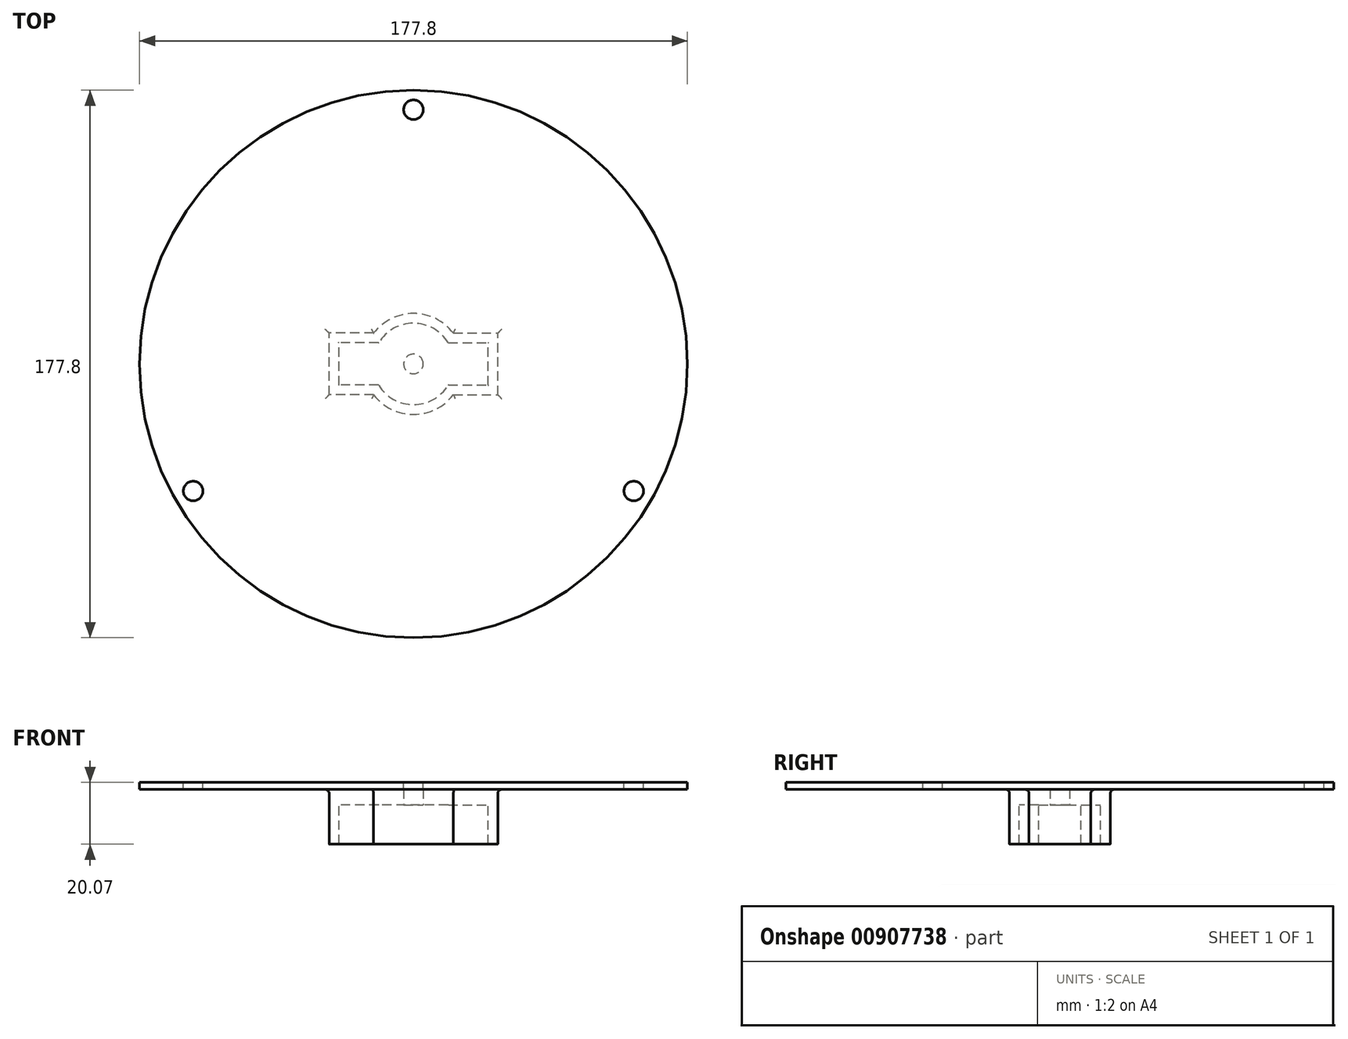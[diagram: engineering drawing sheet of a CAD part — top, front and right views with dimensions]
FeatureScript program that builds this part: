
annotation { "Feature Type Name" : "Feature", "Feature Type Description" : "" }
export const myFeature = defineFeature(function(context is Context, id is Id, definition is map)
    precondition{}
    {
        {
            var Q0;
            Q0=qCreatedBy(makeId("Top.planeOp"),FACE);
            var sketch = newSketch(context, id + "F0", { "sketchPlane" : qUnion([Q0])});
            skCircle(sketch, "E0", {"center": v(0, 0) * mm, "radius": 88.9 * mm});
            skSolve(sketch);
        }
        {
            var Q0;
            Q0=makeQuery(id+"F0.imprint","IMPRINT",FACE,{"disambiguationData":[TD([[makeQuery(id+"F0.imprint","IMPRINT",EDGE,{"derivedFrom":sQuery(id+"F0.wireOp",EDGE,"E0")}),1.0]])]});
            extrude(context, id + "F1", {"entities" : qUnion([Q0]), "depth" : 2.3 * mm, "offsetDistance" : 25.4 * mm});
        }
        {
            var Q0;
            Q0=makeQuery(id+"F1.opExtrude","CAP_FACE",FACE,{"disambiguationData":[OSD([sQuery(id+"F0.wireOp",EDGE,"E0")])],"isStart":false});
            var sketch = newSketch(context, id + "F2", { "sketchPlane" : qUnion([Q0])});
            skCircle(sketch, "E1", {"center": v(0, 82.55) * mm, "radius": 3.18 * mm});
            skCircle(sketch, "E2.1.0", {"center": v(-71.5, -41.27) * mm, "radius": 3.18 * mm});
            skCircle(sketch, "E2.2.0", {"center": v(71.5, -41.28) * mm, "radius": 3.18 * mm});
            skPoint(sketch, "E2.center", {"position": v(0, 0) * mm});
            skSolve(sketch);
        }
        {
            var Q0;
            Q0 = qSketchRegion(id + "F2", true);
            extrude(context, id + "F3", {"entities" : qUnion([Q0]), "operationType" : NewBodyOperationType.REMOVE, "oppositeDirection" : true, "depth" : 25.4 * mm, "offsetDistance" : 25.4 * mm});
        }
        {
            var Q0;
            Q0=makeQuery(id+"F1.opExtrude","CAP_FACE",FACE,{"disambiguationData":[OSD([sQuery(id+"F0.wireOp",EDGE,"E0")])],"isStart":true});
            var sketch = newSketch(context, id + "F4", { "sketchPlane" : qUnion([Q0])});
            skArc(sketch, "E3", {"start": v(0, 12.7) * mm, "mid": v(-6.35, 11) * mm, "end": v(-11, 6.35) * mm});
            skLineSegment(sketch, "E4.bottom", {"start": v(-11, 6.35) * mm, "end": v(-23.7, 6.35) * mm});
            skLineSegment(sketch, "E4.top", {"start": v(-11, -6.35) * mm, "end": v(-23.7, -6.35) * mm});
            skLineSegment(sketch, "E4.right", {"start": v(-23.7, 6.35) * mm, "end": v(-23.7, -6.35) * mm});
            skArc(sketch, "E5.trimOffspring", {"start": v(-11, -6.35) * mm, "mid": v(-6.35, -11) * mm, "end": v(0, -12.7) * mm});
            skArc(sketch, "E6.MirrorCS", {"start": v(0, 12.7) * mm, "mid": v(6.35, 11) * mm, "end": v(11, 6.35) * mm});
            skLineSegment(sketch, "E7.MirrorCS", {"start": v(11, 6.35) * mm, "end": v(23.7, 6.35) * mm});
            skLineSegment(sketch, "E8.MirrorCS", {"start": v(23.7, 6.35) * mm, "end": v(23.7, -6.35) * mm});
            skLineSegment(sketch, "E9.MirrorCS", {"start": v(11, -6.35) * mm, "end": v(23.7, -6.35) * mm});
            skArc(sketch, "E10.MirrorCS", {"start": v(11, -6.35) * mm, "mid": v(6.35, -11) * mm, "end": v(0, -12.7) * mm});
            skArc(sketch, "E11.0", {"start": v(0, 13.2) * mm, "mid": v(-6.48, 11.51) * mm, "end": v(-11.29, 6.86) * mm});
            skArc(sketch, "E11.1", {"start": v(0, 13.2) * mm, "mid": v(6.48, 11.51) * mm, "end": v(11.29, 6.86) * mm});
            skLineSegment(sketch, "E11.2", {"start": v(-11.29, 6.86) * mm, "end": v(-24.2, 6.86) * mm});
            skLineSegment(sketch, "E11.3", {"start": v(11.29, 6.86) * mm, "end": v(24.2, 6.86) * mm});
            skLineSegment(sketch, "E11.4", {"start": v(24.2, 6.86) * mm, "end": v(24.2, -6.86) * mm});
            skLineSegment(sketch, "E11.5", {"start": v(11.29, -6.86) * mm, "end": v(24.2, -6.86) * mm});
            skLineSegment(sketch, "E11.6", {"start": v(-24.2, 6.86) * mm, "end": v(-24.2, -6.86) * mm});
            skLineSegment(sketch, "E11.7", {"start": v(-11.29, -6.86) * mm, "end": v(-24.2, -6.86) * mm});
            skArc(sketch, "E11.8", {"start": v(-11.29, -6.86) * mm, "mid": v(-6.48, -11.51) * mm, "end": v(0, -13.2) * mm});
            skArc(sketch, "E11.9", {"start": v(11.29, -6.86) * mm, "mid": v(6.48, -11.51) * mm, "end": v(0, -13.2) * mm});
            skArc(sketch, "E12.0", {"start": v(0, 16.38) * mm, "mid": v(-7.21, 14.7) * mm, "end": v(-12.95, 10.03) * mm});
            skArc(sketch, "E12.1", {"start": v(0, 16.38) * mm, "mid": v(7.21, 14.7) * mm, "end": v(12.95, 10.03) * mm});
            skLineSegment(sketch, "E12.2", {"start": v(-12.95, 10.03) * mm, "end": v(-27.37, 10.03) * mm});
            skLineSegment(sketch, "E12.3", {"start": v(12.95, 10.03) * mm, "end": v(27.37, 10.03) * mm});
            skLineSegment(sketch, "E12.4", {"start": v(27.37, 10.03) * mm, "end": v(27.37, -10.03) * mm});
            skLineSegment(sketch, "E12.5", {"start": v(12.95, -10.03) * mm, "end": v(27.37, -10.03) * mm});
            skLineSegment(sketch, "E12.6", {"start": v(-27.37, 10.03) * mm, "end": v(-27.37, -10.03) * mm});
            skLineSegment(sketch, "E12.7", {"start": v(-12.95, -10.03) * mm, "end": v(-27.37, -10.03) * mm});
            skArc(sketch, "E12.8", {"start": v(-12.95, -10.03) * mm, "mid": v(-7.21, -14.7) * mm, "end": v(0, -16.38) * mm});
            skArc(sketch, "E12.9", {"start": v(12.95, -10.03) * mm, "mid": v(7.21, -14.7) * mm, "end": v(0, -16.38) * mm});
            skSolve(sketch);
        }
        {
            var Q0;
            Q0=makeQuery(id+"F4.imprint","IMPRINT",FACE,{"disambiguationData":[TD([[makeQuery(id+"F4.imprint","IMPRINT",EDGE,{"derivedFrom":sQuery(id+"F4.wireOp",EDGE,"E11.0")}),-1.0]])]});
            extrude(context, id + "F5", {"entities" : qUnion([Q0]), "operationType" : NewBodyOperationType.ADD, "depth" : 17.78 * mm, "offsetDistance" : 25.4 * mm});
        }
        {
            var Q0;
            Q0=makeQuery(id+"F5.boolean.opBoolean","SPLIT",FACE,{"disambiguationData":[TD([makeQuery(id+"F5.opExtrude","SWEPT_FACE",FACE,{"disambiguationData":[OSD([sQuery(id+"F4.wireOp",EDGE,"E11.2")])]})])],"derivedFrom":makeQuery(id+"F1.opExtrude","CAP_FACE",FACE,{"disambiguationData":[OSD([sQuery(id+"F0.wireOp",EDGE,"E0")])],"isStart":true})});
            extrude(context, id + "F6", {"entities" : qUnion([Q0]), "operationType" : NewBodyOperationType.ADD, "depth" : 5.08 * mm, "offsetDistance" : 25.4 * mm});
        }
        {
            var Q0;
            Q0=makeQuery(id+"F6.opExtrude","CAP_FACE",FACE,{"disambiguationData":[OSD([sQuery(id+"F0.wireOp",EDGE,"E0")])],"isStart":false});
            var sketch = newSketch(context, id + "F7", { "sketchPlane" : qUnion([Q0])});
            skCircle(sketch, "E13", {"center": v(0, 0) * mm, "radius": 3.18 * mm});
            skSolve(sketch);
        }
        {
            var Q0;
            Q0 = qSketchRegion(id + "F7", true);
            extrude(context, id + "F8", {"entities" : qUnion([Q0]), "operationType" : NewBodyOperationType.REMOVE, "oppositeDirection" : true, "depth" : 5.08 * mm, "offsetDistance" : 25.4 * mm});
        }
        {
            var Q0;
            Q0=makeQuery(id+"F5.opExtrude","SWEPT_EDGE",EDGE,{"disambiguationData":[OSD([sQuery(id+"F4.wireOp",EDGE,"E11.1"),sQuery(id+"F4.wireOp",EDGE,"E11.3")])]});
            var Q1;
            Q1=makeQuery(id+"F5.opExtrude","SWEPT_EDGE",EDGE,{"disambiguationData":[OSD([sQuery(id+"F4.wireOp",EDGE,"E11.0"),sQuery(id+"F4.wireOp",EDGE,"E11.2")])]});
            var Q2;
            Q2=makeQuery(id+"F5.opExtrude","SWEPT_EDGE",EDGE,{"disambiguationData":[OSD([sQuery(id+"F4.wireOp",EDGE,"E11.5"),sQuery(id+"F4.wireOp",EDGE,"E11.9")])]});
            var Q3;
            Q3=makeQuery(id+"F5.opExtrude","SWEPT_EDGE",EDGE,{"disambiguationData":[OSD([sQuery(id+"F4.wireOp",EDGE,"E11.7"),sQuery(id+"F4.wireOp",EDGE,"E11.8")])]});
            var Q4;
            Q4=makeQuery(id+"F5.opExtrude","CAP_FACE",FACE,{"disambiguationData":[OSD([sQuery(id+"F4.wireOp",EDGE,"E11.0"),sQuery(id+"F4.wireOp",EDGE,"E11.1"),sQuery(id+"F4.wireOp",EDGE,"E11.2"),sQuery(id+"F4.wireOp",EDGE,"E11.3"),sQuery(id+"F4.wireOp",EDGE,"E11.4"),sQuery(id+"F4.wireOp",EDGE,"E11.5"),sQuery(id+"F4.wireOp",EDGE,"E11.6"),sQuery(id+"F4.wireOp",EDGE,"E11.7"),sQuery(id+"F4.wireOp",EDGE,"E11.8"),sQuery(id+"F4.wireOp",EDGE,"E11.9"),sQuery(id+"F4.wireOp",EDGE,"E12.0"),sQuery(id+"F4.wireOp",EDGE,"E12.1"),sQuery(id+"F4.wireOp",EDGE,"E12.2"),sQuery(id+"F4.wireOp",EDGE,"E12.3"),sQuery(id+"F4.wireOp",EDGE,"E12.4"),sQuery(id+"F4.wireOp",EDGE,"E12.5"),sQuery(id+"F4.wireOp",EDGE,"E12.6"),sQuery(id+"F4.wireOp",EDGE,"E12.7"),sQuery(id+"F4.wireOp",EDGE,"E12.8"),sQuery(id+"F4.wireOp",EDGE,"E12.9")])],"isStart":false});
            fillet(context, id + "F9", {"entities" : qUnion([Q0, Q1, Q2, Q3, Q4]), "radius" : 0.13 * mm, "tangentPropagation" : true, "allowEdgeOverflow" : false});
        }
        {
            var Q0;
            Q0=makeQuery(id+"F5.opExtrude","CAP_EDGE",EDGE,{"disambiguationData":[OSD([sQuery(id+"F4.wireOp",EDGE,"E12.4")])],"isStart":true});
            var Q1;
            Q1=makeQuery(id+"F5.opExtrude","CAP_EDGE",EDGE,{"disambiguationData":[OSD([sQuery(id+"F4.wireOp",EDGE,"E12.3")])],"isStart":true});
            var Q2;
            Q2=makeQuery(id+"F5.opExtrude","CAP_EDGE",EDGE,{"disambiguationData":[OSD([sQuery(id+"F4.wireOp",EDGE,"E12.5")])],"isStart":true});
            var Q3;
            Q3=makeQuery(id+"F5.opExtrude","CAP_EDGE",EDGE,{"disambiguationData":[OSD([sQuery(id+"F4.wireOp",EDGE,"E12.8"),sQuery(id+"F4.wireOp",EDGE,"E12.9")])],"isStart":true});
            var Q4;
            Q4=makeQuery(id+"F5.opExtrude","CAP_EDGE",EDGE,{"disambiguationData":[OSD([sQuery(id+"F4.wireOp",EDGE,"E12.7")])],"isStart":true});
            var Q5;
            Q5=makeQuery(id+"F5.opExtrude","CAP_EDGE",EDGE,{"disambiguationData":[OSD([sQuery(id+"F4.wireOp",EDGE,"E12.6")])],"isStart":true});
            var Q6;
            Q6=makeQuery(id+"F5.opExtrude","CAP_EDGE",EDGE,{"disambiguationData":[OSD([sQuery(id+"F4.wireOp",EDGE,"E12.0"),sQuery(id+"F4.wireOp",EDGE,"E12.1")])],"isStart":true});
            var Q7;
            Q7=makeQuery(id+"F5.opExtrude","CAP_EDGE",EDGE,{"disambiguationData":[OSD([sQuery(id+"F4.wireOp",EDGE,"E12.2")])],"isStart":true});
            fillet(context, id + "F10", {"entities" : qUnion([Q0, Q1, Q2, Q3, Q4, Q5, Q6, Q7]), "radius" : 1.27 * mm, "tangentPropagation" : true, "allowEdgeOverflow" : false});
        }
    });
